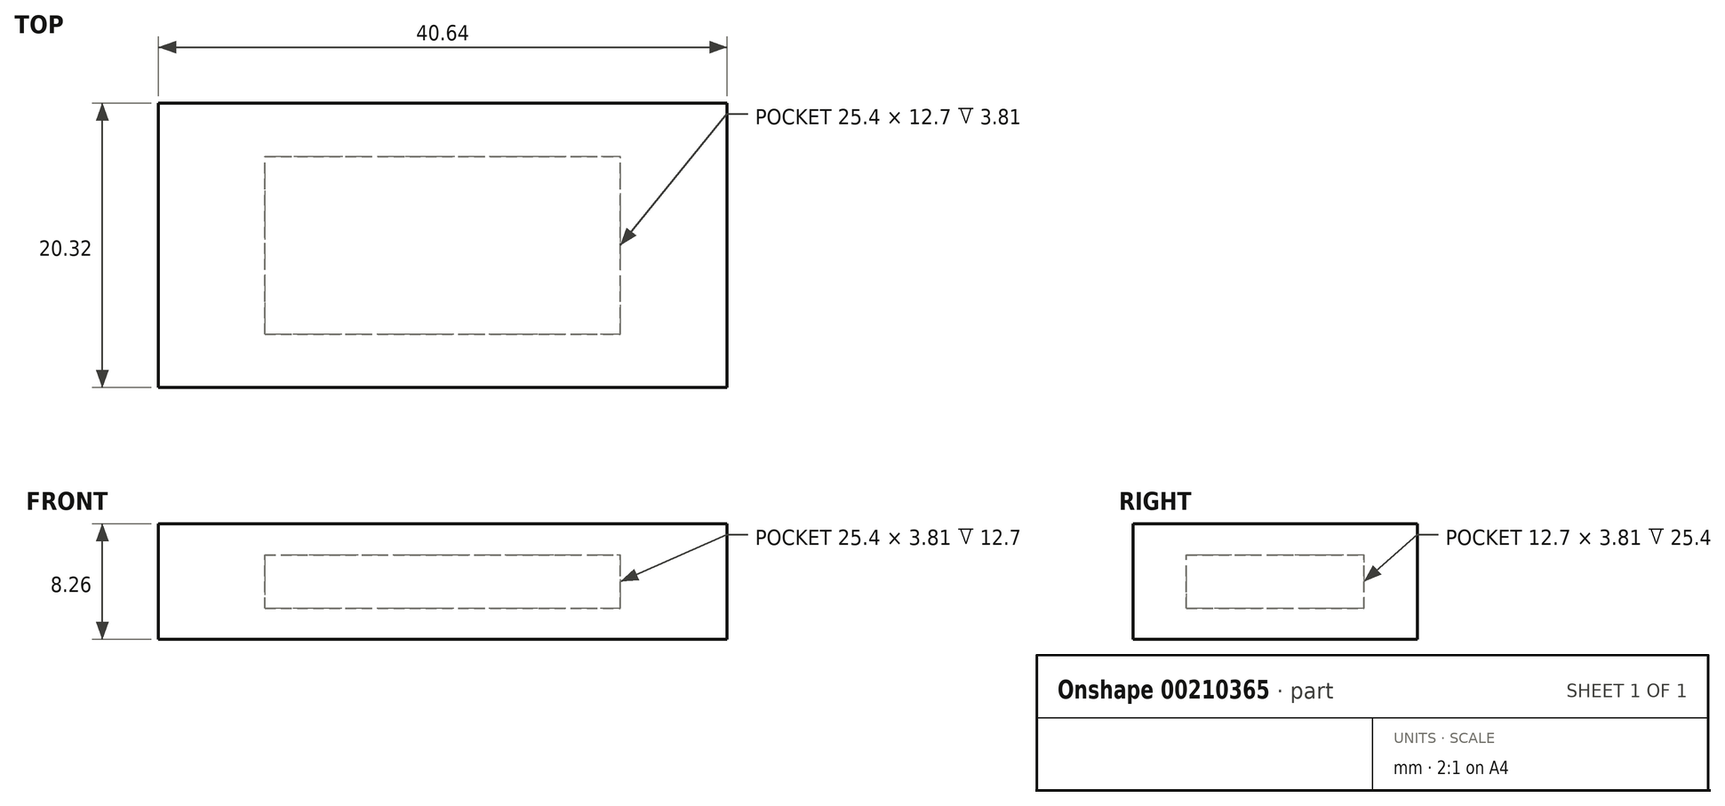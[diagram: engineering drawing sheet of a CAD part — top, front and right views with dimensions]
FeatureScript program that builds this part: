
annotation { "Feature Type Name" : "Feature", "Feature Type Description" : "" }
export const myFeature = defineFeature(function(context is Context, id is Id, definition is map)
    precondition{}
    {
        {
            var Q0;
            Q0=qCreatedBy(makeId("Top.planeOp"),FACE);
            var sketch = newSketch(context, id + "F0", { "sketchPlane" : qUnion([Q0])});
            skLineSegment(sketch, "E0.bottom", {"start": v(-20.32, 10.16) * mm, "end": v(20.32, 10.16) * mm});
            skLineSegment(sketch, "E0.top", {"start": v(-20.32, -10.16) * mm, "end": v(20.32, -10.16) * mm});
            skLineSegment(sketch, "E0.left", {"start": v(-20.32, 10.16) * mm, "end": v(-20.32, -10.16) * mm});
            skLineSegment(sketch, "E0.right", {"start": v(20.32, 10.16) * mm, "end": v(20.32, -10.16) * mm});
            skLineSegment(sketch, "E1", {"start": v(-20.32, -10.16) * mm, "end": v(20.32, 10.16) * mm, "construction": true});
            skPoint(sketch, "E2", {"position": v(0, 0) * mm});
            skSolve(sketch);
        }
        {
            var Q0;
            Q0 = qSketchRegion(id + "F0", true);
            extrude(context, id + "F1", {"entities" : qUnion([Q0]), "endBound" : BoundingType.SYMMETRIC, "depth" : 8.25 * mm, "offsetDistance" : 25.4 * mm});
        }
        {
            var Q0;
            Q0=qCreatedBy(makeId("Top.planeOp"),FACE);
            var sketch = newSketch(context, id + "F2", { "sketchPlane" : qUnion([Q0])});
            skLineSegment(sketch, "E3.bottom", {"start": v(-12.7, -6.35) * mm, "end": v(12.7, -6.35) * mm});
            skLineSegment(sketch, "E3.top", {"start": v(-12.7, 6.35) * mm, "end": v(12.7, 6.35) * mm});
            skLineSegment(sketch, "E3.left", {"start": v(-12.7, -6.35) * mm, "end": v(-12.7, 6.35) * mm});
            skLineSegment(sketch, "E3.right", {"start": v(12.7, -6.35) * mm, "end": v(12.7, 6.35) * mm});
            skLineSegment(sketch, "E4", {"start": v(-12.7, -6.35) * mm, "end": v(12.7, 6.35) * mm, "construction": true});
            skPoint(sketch, "E5", {"position": v(0, 0) * mm});
            skSolve(sketch);
        }
        {
            var Q0;
            Q0 = qSketchRegion(id + "F2", true);
            extrude(context, id + "F3", {"entities" : qUnion([Q0]), "operationType" : NewBodyOperationType.REMOVE, "endBound" : BoundingType.SYMMETRIC, "oppositeDirection" : true, "depth" : 3.8 * mm, "offsetDistance" : 25.4 * mm});
        }
    });
